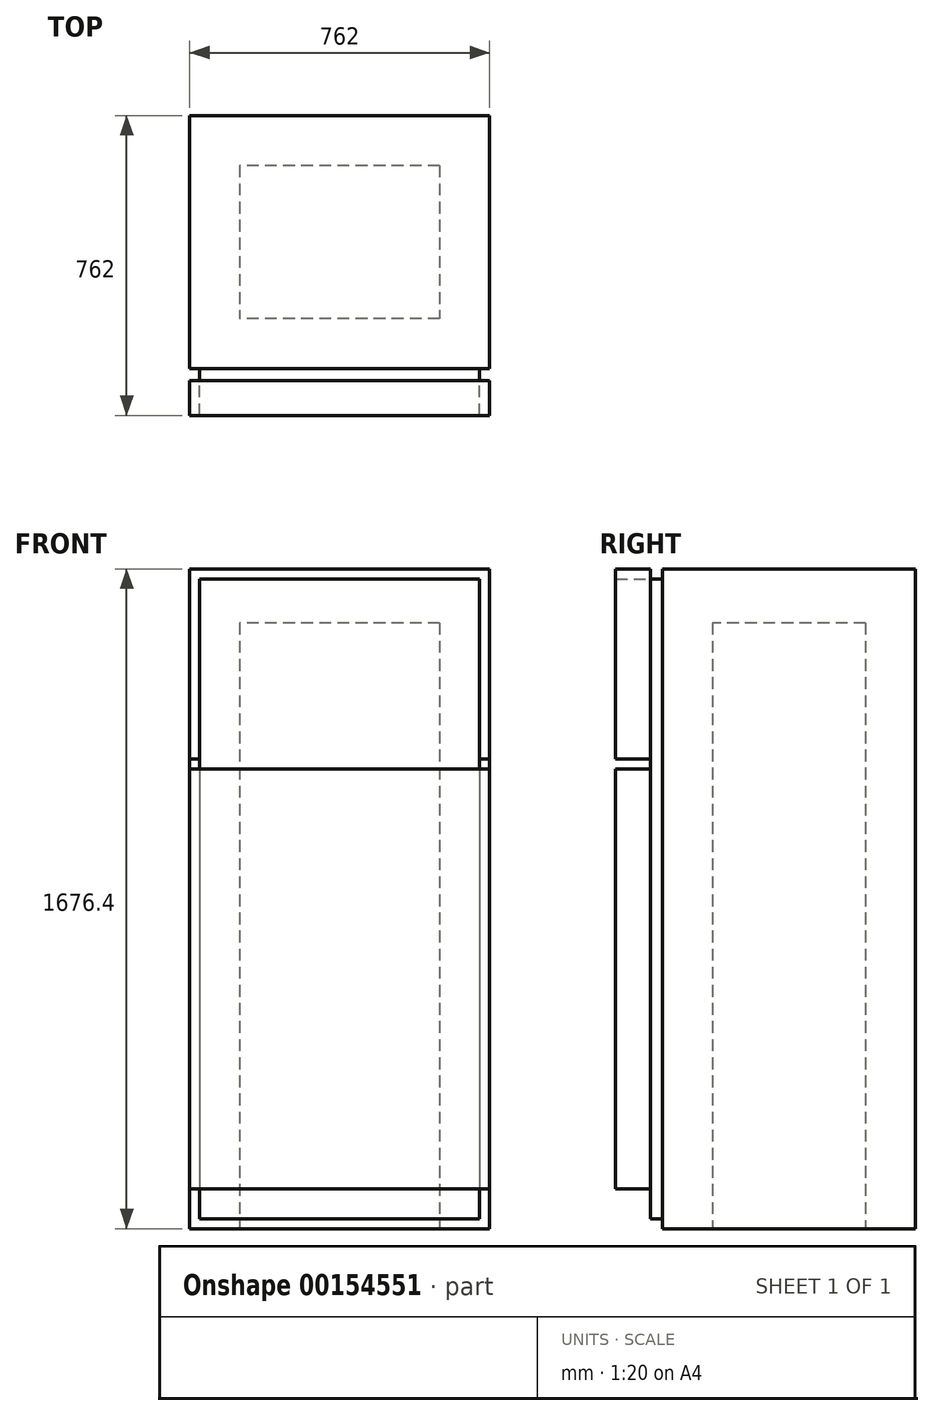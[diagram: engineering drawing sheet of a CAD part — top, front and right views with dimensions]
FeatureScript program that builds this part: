
annotation { "Feature Type Name" : "Feature", "Feature Type Description" : "" }
export const myFeature = defineFeature(function(context is Context, id is Id, definition is map)
    precondition{}
    {
        {
            var Q0;
            Q0=qCreatedBy(makeId("Top.planeOp"),FACE);
            var sketch = newSketch(context, id + "F0", { "sketchPlane" : qUnion([Q0])});
            skLineSegment(sketch, "E0.bottom", {"start": v(381, 336.55) * mm, "end": v(-381, 336.55) * mm});
            skLineSegment(sketch, "E0.top", {"start": v(381, -336.55) * mm, "end": v(-381, -336.55) * mm});
            skLineSegment(sketch, "E0.left", {"start": v(381, 336.55) * mm, "end": v(381, -336.55) * mm});
            skLineSegment(sketch, "E0.right", {"start": v(-381, 336.55) * mm, "end": v(-381, -336.55) * mm});
            skPoint(sketch, "E0.middle", {"position": v(0, 0) * mm});
            skSolve(sketch);
        }
        {
            var Q0;
            Q0=makeQuery(id+"F0.imprint","IMPRINT",FACE,{"disambiguationData":[TD([[makeQuery(id+"F0.imprint","IMPRINT",EDGE,{"derivedFrom":sQuery(id+"F0.wireOp",EDGE,"E0.bottom")}),1.0]])]});
            extrude(context, id + "F1", {"entities" : qUnion([Q0]), "depth" : 1676.4 * mm});
        }
        {
            var Q0;
            Q0=makeQuery(id+"F1.opExtrude","SWEPT_FACE",FACE,{"disambiguationData":[OSD([sQuery(id+"F0.wireOp",EDGE,"E0.top")])]});
            var sketch = newSketch(context, id + "F2", { "sketchPlane" : qUnion([Q0])});
            skLineSegment(sketch, "E1.0", {"start": v(355.6, 1651) * mm, "end": v(-355.6, 1651) * mm});
            skLineSegment(sketch, "E1.1", {"start": v(355.6, 1651) * mm, "end": v(355.6, 25.4) * mm});
            skLineSegment(sketch, "E1.2", {"start": v(355.6, 25.4) * mm, "end": v(-355.6, 25.4) * mm});
            skLineSegment(sketch, "E1.3", {"start": v(-355.6, 1651) * mm, "end": v(-355.6, 25.4) * mm});
            skSolve(sketch);
        }
        {
            var Q0;
            Q0=makeQuery(id+"F2.imprint","IMPRINT",FACE,{"disambiguationData":[TD([[makeQuery(id+"F2.imprint","IMPRINT",EDGE,{"derivedFrom":sQuery(id+"F2.wireOp",EDGE,"E1.0")}),-1.0]])]});
            extrude(context, id + "F3", {"entities" : qUnion([Q0]), "operationType" : NewBodyOperationType.REMOVE, "oppositeDirection" : true, "depth" : 30.48 * mm});
        }
        {
            var Q0;
            Q0=makeQuery(id+"F1.opExtrude","SWEPT_FACE",FACE,{"disambiguationData":[OSD([sQuery(id+"F0.wireOp",EDGE,"E0.top")])]});
            var sketch = newSketch(context, id + "F4", { "sketchPlane" : qUnion([Q0])});
            skLineSegment(sketch, "E2.bottom", {"start": v(-381, 1676.4) * mm, "end": v(381, 1676.4) * mm});
            skLineSegment(sketch, "E2.top", {"start": v(-381, 1193.8) * mm, "end": v(381, 1193.8) * mm});
            skLineSegment(sketch, "E2.left", {"start": v(-381, 1676.4) * mm, "end": v(-381, 1193.8) * mm});
            skLineSegment(sketch, "E2.right", {"start": v(381, 1676.4) * mm, "end": v(381, 1193.8) * mm});
            skLineSegment(sketch, "E3.bottom", {"start": v(-381, 1168.4) * mm, "end": v(381, 1168.4) * mm});
            skLineSegment(sketch, "E3.top", {"start": v(-381, 101.6) * mm, "end": v(381, 101.6) * mm});
            skLineSegment(sketch, "E3.left", {"start": v(-381, 1168.4) * mm, "end": v(-381, 101.6) * mm});
            skLineSegment(sketch, "E3.right", {"start": v(381, 1168.4) * mm, "end": v(381, 101.6) * mm});
            skSolve(sketch);
        }
        {
            var Q0;
            {var subQ5=makeQuery(id+"F3.boolean.opBoolean","COPY",EDGE,{"derivedFrom":makeQuery(id+"F3.opExtrude","CAP_EDGE",EDGE,{"disambiguationData":[OSD([sQuery(id+"F2.wireOp",EDGE,"E1.0")])],"isStart":true})});Q0=makeQuery(id+"F4.imprint","IMPRINT",FACE,{"disambiguationData":[TD([[makeQuery(id+"F4.imprint","IMPRINT",EDGE,{"derivedFrom":subQ5}),1.0]])]});}
            var Q1;
            Q1=makeQuery(id+"F4.imprint","IMPRINT",FACE,{"disambiguationData":[TD([[makeQuery(id+"F4.imprint","IMPRINT",EDGE,{"derivedFrom":sQuery(id+"F4.wireOp",EDGE,"E2.bottom")}),-1.0]])]});
            var Q2;
            {var subQ0=sQuery(id+"F4.wireOp",EDGE,"E3.right");Q2=makeQuery(id+"F4.imprint","IMPRINT",FACE,{"disambiguationData":[TD([[makeQuery(id+"F4.imprint","IMPRINT",EDGE,{"derivedFrom":subQ0}),-1.0]])]});}
            var Q3;
            {var subQ0=sQuery(id+"F4.wireOp",EDGE,"E3.bottom");var subQ1=makeQuery(id+"F3.boolean.opBoolean","COPY",EDGE,{"derivedFrom":makeQuery(id+"F3.opExtrude","CAP_EDGE",EDGE,{"disambiguationData":[OSD([sQuery(id+"F2.wireOp",EDGE,"E1.3")])],"isStart":true})});var subQ2=makeQuery(id+"F4.imprint","INTERSECT",VERTEX,{"derivedFrom":[subQ1,subQ0]});Q3=makeQuery(id+"F4.imprint","IMPRINT",FACE,{"disambiguationData":[TD([[makeQuery(id+"F4.imprint","IMPRINT",EDGE,{"disambiguationData":[TD([[subQ2,-1.0]])],"derivedFrom":subQ0}),-1.0]])]});}
            var Q4;
            {var subQ0=sQuery(id+"F4.wireOp",EDGE,"E3.left");Q4=makeQuery(id+"F4.imprint","IMPRINT",FACE,{"disambiguationData":[TD([[makeQuery(id+"F4.imprint","IMPRINT",EDGE,{"derivedFrom":subQ0}),1.0]])]});}
            extrude(context, id + "F5", {"entities" : qUnion([Q0, Q1, Q2, Q3, Q4]), "operationType" : NewBodyOperationType.ADD, "depth" : 88.9 * mm});
        }
        {
            var Q0;
            Q0=makeQuery(id+"F1.opExtrude","CAP_FACE",FACE,{"disambiguationData":[OSD([sQuery(id+"F0.wireOp",EDGE,"E0.bottom"),sQuery(id+"F0.wireOp",EDGE,"E0.top"),sQuery(id+"F0.wireOp",EDGE,"E0.left"),sQuery(id+"F0.wireOp",EDGE,"E0.right")])],"isStart":true});
            var sketch = newSketch(context, id + "F6", { "sketchPlane" : qUnion([Q0])});
            skLineSegment(sketch, "E4.0", {"start": v(254, -209.55) * mm, "end": v(254, 179.07) * mm});
            skLineSegment(sketch, "E4.1", {"start": v(254, -209.55) * mm, "end": v(-254, -209.55) * mm});
            skLineSegment(sketch, "E4.2", {"start": v(-254, -209.55) * mm, "end": v(-254, 179.07) * mm});
            skLineSegment(sketch, "E4.3", {"start": v(254, 179.07) * mm, "end": v(-254, 179.07) * mm});
            skSolve(sketch);
        }
        {
            var Q0;
            Q0=makeQuery(id+"F6.imprint","IMPRINT",FACE,{"disambiguationData":[TD([[makeQuery(id+"F6.imprint","IMPRINT",EDGE,{"derivedFrom":sQuery(id+"F6.wireOp",EDGE,"E4.0")}),1.0]])]});
            extrude(context, id + "F7", {"entities" : qUnion([Q0]), "operationType" : NewBodyOperationType.REMOVE, "oppositeDirection" : true, "depth" : 1539.24 * mm});
        }
    });
